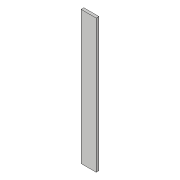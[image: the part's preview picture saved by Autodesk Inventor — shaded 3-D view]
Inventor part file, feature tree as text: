
AUTODESK INVENTOR PART (.ipt)
format: ipt  version: 2018.3 (Build 223284000, 284)  size: 72,192 bytes
history: native  units: in
note: dims shown in document units (in); Inventor stores cm internally (conversion verified against a paired STEP export)
features: extrude x1, sketch x1
ambient origin geometry x8: Origin, YZ Plane, XZ Plane, XY Plane, X Axis, Y Axis, Z Axis, Center Point
bodies: Solid1 (feature_tree)
feature tree (2):
  extrude  "Extrusion1"  Depth=0.675in
  sketch  "Sketch1"  dims[d0=6.0in d1=0.675in d2=0.125in d3=0.0in]
